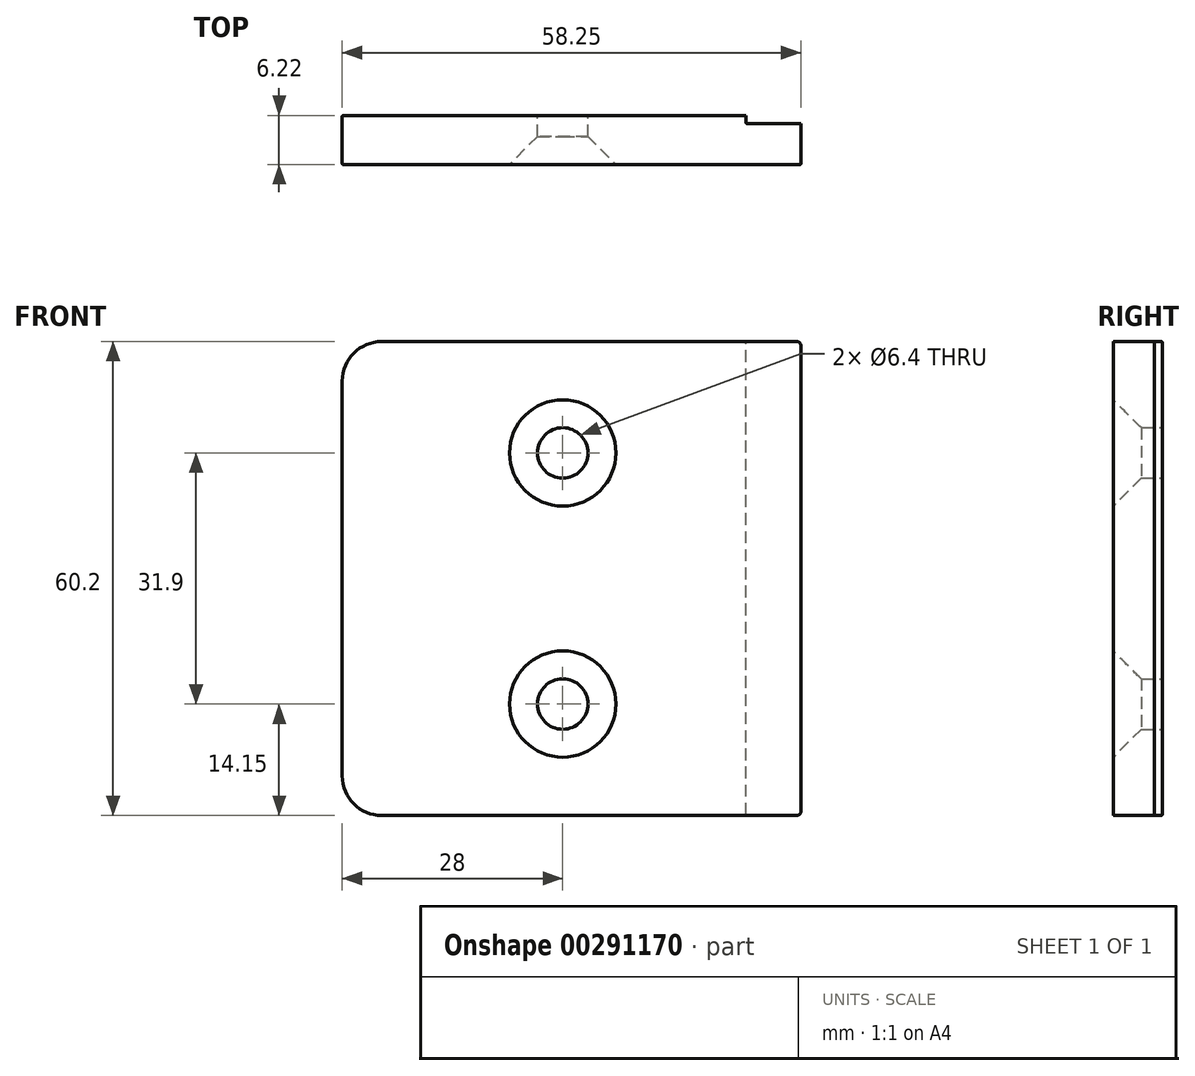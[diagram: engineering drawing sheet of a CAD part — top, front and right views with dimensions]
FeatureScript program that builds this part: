
annotation { "Feature Type Name" : "Feature", "Feature Type Description" : "" }
export const myFeature = defineFeature(function(context is Context, id is Id, definition is map)
    precondition{}
    {
        {
            var Q0;
            Q0=qCreatedBy(makeId("Front.planeOp"),FACE);
            var sketch = newSketch(context, id + "F0", { "sketchPlane" : qUnion([Q0])});
            skLineSegment(sketch, "E0.bottom", {"start": v(-0.5, 0) * mm, "end": v(-53.25, 0) * mm});
            skLineSegment(sketch, "E0.top", {"start": v(-0.5, 60.2) * mm, "end": v(-53.25, 60.2) * mm});
            skLineSegment(sketch, "E0.left", {"start": v(0, 0.5) * mm, "end": v(0, 59.7) * mm});
            skLineSegment(sketch, "E0.right", {"start": v(-58.25, 5) * mm, "end": v(-58.25, 55.2) * mm});
            skPoint(sketch, "E1.visualSharp", {"position": v(-58.25, 60.2) * mm});
            skArc(sketch, "E1.filletArc", {"start": v(-53.25, 60.2) * mm, "mid": v(-56.79, 58.74) * mm, "end": v(-58.25, 55.2) * mm});
            skPoint(sketch, "E2.visualSharp", {"position": v(-58.25, 0) * mm});
            skArc(sketch, "E2.filletArc", {"start": v(-58.25, 5) * mm, "mid": v(-56.79, 1.46) * mm, "end": v(-53.25, 0) * mm});
            skPoint(sketch, "E3.visualSharp", {"position": v(0, 0) * mm});
            skArc(sketch, "E3.filletArc", {"start": v(-0.5, 0) * mm, "mid": v(-0.15, 0.15) * mm, "end": v(0, 0.5) * mm});
            skPoint(sketch, "E4.visualSharp", {"position": v(0, 60.2) * mm});
            skArc(sketch, "E4.filletArc", {"start": v(0, 59.7) * mm, "mid": v(-0.15, 60.05) * mm, "end": v(-0.5, 60.2) * mm});
            skSolve(sketch);
        }
        {
            var Q0;
            Q0=makeQuery(id+"F0.imprint","IMPRINT",FACE,{"disambiguationData":[TD([[makeQuery(id+"F0.imprint","IMPRINT",EDGE,{"derivedFrom":sQuery(id+"F0.wireOp",EDGE,"E0.bottom")}),-1.0]])]});
            extrude(context, id + "F1", {"entities" : qUnion([Q0]), "depth" : 6.22 * mm});
        }
        {
            var Q0;
            Q0=makeQuery(id+"F1.opExtrude","SWEPT_FACE",FACE,{"disambiguationData":[OSD([sQuery(id+"F0.wireOp",EDGE,"E0.top")])]});
            var sketch = newSketch(context, id + "F2", { "sketchPlane" : qUnion([Q0])});
            skLineSegment(sketch, "E5.bottom", {"start": v(0, 0) * mm, "end": v(-7, 0) * mm});
            skLineSegment(sketch, "E5.top", {"start": v(0, -1) * mm, "end": v(-7, -1) * mm});
            skLineSegment(sketch, "E5.left", {"start": v(0, 0) * mm, "end": v(0, -1) * mm});
            skLineSegment(sketch, "E5.right", {"start": v(-7, 0) * mm, "end": v(-7, -1) * mm});
            skSolve(sketch);
        }
        {
            var Q0;
            Q0=qSketchRegion(id+"F2",true);
            extrude(context, id + "F3", {"entities" : qUnion([Q0]), "operationType" : NewBodyOperationType.REMOVE, "endBound" : BoundingType.THROUGH_ALL, "oppositeDirection" : true, "depth" : 25 * mm});
        }
        {
            var Q0;
            Q0=makeQuery(id+"F1.opExtrude","CAP_EDGE",EDGE,{"disambiguationData":[OSD([sQuery(id+"F0.wireOp",EDGE,"E0.top")])],"isStart":false});
            var Q1;
            Q1=makeQuery(id+"F1.opExtrude","CAP_EDGE",EDGE,{"disambiguationData":[OSD([sQuery(id+"F0.wireOp",EDGE,"E0.top")])],"isStart":true});
            var Q2;
            Q2=makeQuery(id+"F3.boolean.opBoolean","COPY",EDGE,{"derivedFrom":makeQuery(id+"F3.opExtrude","SWEPT_EDGE",EDGE,{"disambiguationData":[OSD([sQuery(id+"F0.wireOp",EDGE,"E0.top"),sQuery(id+"F2.wireOp",EDGE,"E5.bottom"),sQuery(id+"F2.wireOp",EDGE,"E5.right")])]})});
            var Q3;
            Q3=makeQuery(id+"F3.boolean.opBoolean","COPY",EDGE,{"derivedFrom":makeQuery(id+"F3.opExtrude","CAP_EDGE",EDGE,{"disambiguationData":[OSD([sQuery(id+"F2.wireOp",EDGE,"E5.top")])],"isStart":true})});
            var Q4;
            Q4=makeQuery(id+"F3.boolean.opBoolean","COPY",EDGE,{"derivedFrom":makeQuery(id+"F3.opExtrude","CAP_EDGE",EDGE,{"disambiguationData":[OSD([sQuery(id+"F2.wireOp",EDGE,"E5.right")])],"isStart":true})});
            var Q5;
            Q5=makeQuery(id+"F3.boolean.opBoolean","INTERSECT",EDGE,{"derivedFrom":[makeQuery(id+"F1.opExtrude","SWEPT_FACE",FACE,{"disambiguationData":[OSD([sQuery(id+"F0.wireOp",EDGE,"E0.bottom")])]}),makeQuery(id+"F3.opExtrude","SWEPT_FACE",FACE,{"disambiguationData":[OSD([sQuery(id+"F2.wireOp",EDGE,"E5.right")])]})]});
            var Q6;
            Q6=makeQuery(id+"F3.boolean.opBoolean","COPY",EDGE,{"derivedFrom":makeQuery(id+"F3.opExtrude","SWEPT_EDGE",EDGE,{"disambiguationData":[OSD([sQuery(id+"F2.wireOp",EDGE,"E5.top"),sQuery(id+"F2.wireOp",EDGE,"E5.right")])]})});
            fillet(context, id + "F4", {"entities" : qUnion([Q0, Q1, Q2, Q3, Q4, Q5, Q6]), "radius" : 0.1 * mm, "tangentPropagation" : true, "allowEdgeOverflow" : false});
        }
        {
            var Q0;
            Q0=makeQuery(id+"F1.opExtrude","CAP_FACE",FACE,{"disambiguationData":[OSD([sQuery(id+"F0.wireOp",EDGE,"E0.bottom"),sQuery(id+"F0.wireOp",EDGE,"E0.top"),sQuery(id+"F0.wireOp",EDGE,"E0.left"),sQuery(id+"F0.wireOp",EDGE,"E0.right"),sQuery(id+"F0.wireOp",EDGE,"E1.filletArc"),sQuery(id+"F0.wireOp",EDGE,"E2.filletArc"),sQuery(id+"F0.wireOp",EDGE,"E3.filletArc"),sQuery(id+"F0.wireOp",EDGE,"E4.filletArc")])],"isStart":false});
            var sketch = newSketch(context, id + "F5", { "sketchPlane" : qUnion([Q0])});
            skCircle(sketch, "E6", {"center": v(-30.25, 46.05) * mm, "radius": 3 * mm});
            skCircle(sketch, "E7.MirrorC", {"center": v(-30.25, 14.15) * mm, "radius": 3 * mm});
            skSolve(sketch);
        }
        {
            var Q0;
            Q0=sQuery(id+"F5.wireOp",VERTEX,"E6.center");
            var Q1;
            Q1=sQuery(id+"F5.wireOp",VERTEX,"E7.MirrorC.center");
            var Q2;
            Q2=makeQuery(id+"F1.opExtrude","SWEPT_BODY",BODY,{"disambiguationData":[OSD([sQuery(id+"F0.wireOp",EDGE,"E0.bottom"),sQuery(id+"F0.wireOp",EDGE,"E0.top"),sQuery(id+"F0.wireOp",EDGE,"E0.left"),sQuery(id+"F0.wireOp",EDGE,"E0.right"),sQuery(id+"F0.wireOp",EDGE,"E1.filletArc"),sQuery(id+"F0.wireOp",EDGE,"E2.filletArc"),sQuery(id+"F0.wireOp",EDGE,"E3.filletArc"),sQuery(id+"F0.wireOp",EDGE,"E4.filletArc")])]});
            hole(context, id + "F6", {"style" : HoleStyle.C_SINK, "endStyle" : HoleEndStyle.THROUGH, "holeDiameter" : 6.4 * mm, "cSinkDiameter" : 13.5 * mm, "cSinkAngle" : 90 * degree, "tappedDepth" : 10 * mm, "tapClearance" : 3, "locations" : qUnion([Q0, Q1]), "scope" : qUnion([Q2]), "startStyle" : HoleStartStyle.PART});
        }
    });
